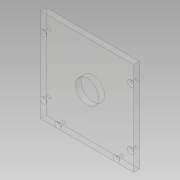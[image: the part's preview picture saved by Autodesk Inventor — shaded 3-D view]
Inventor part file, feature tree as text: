
AUTODESK INVENTOR PART (.ipt)
format: ipt  version: 2019 (Build 230136000, 136)  size: 110,592 bytes
history: native  units: mm
features: sketch x2, other x1, extrude x1, hole x1
ambient origin geometry x8: Origin, YZ Plane, XZ Plane, XY Plane, X Axis, Y Axis, Z Axis, Center Point
bodies: Body1 (feature_tree)
feature tree (5):
  other  "Sólido1"
  extrude  "Extrusión1"  Depth=160.0mm
  hole  "Agujero1"  [1 undecoded]
  sketch  "Boceto1"  dims[d0=160.0mm d1=160.0mm]
  sketch  "Boceto2"  dims[d2=40.0mm d3=10.0mm d4=0.0mm d8=5.5mm d9=6.0mm d10=11.0mm d11=2.0mm d12=90.0deg d13=20.0mm d14=20.594885mm d15=5.0mm d16=30.0mm d17=30.0mm]
note: 1 required parameter value undecoded (feature->parameter linkage not recoverable at this tier; creation-order binding heuristic only, values carry confidence <= 0.55)
